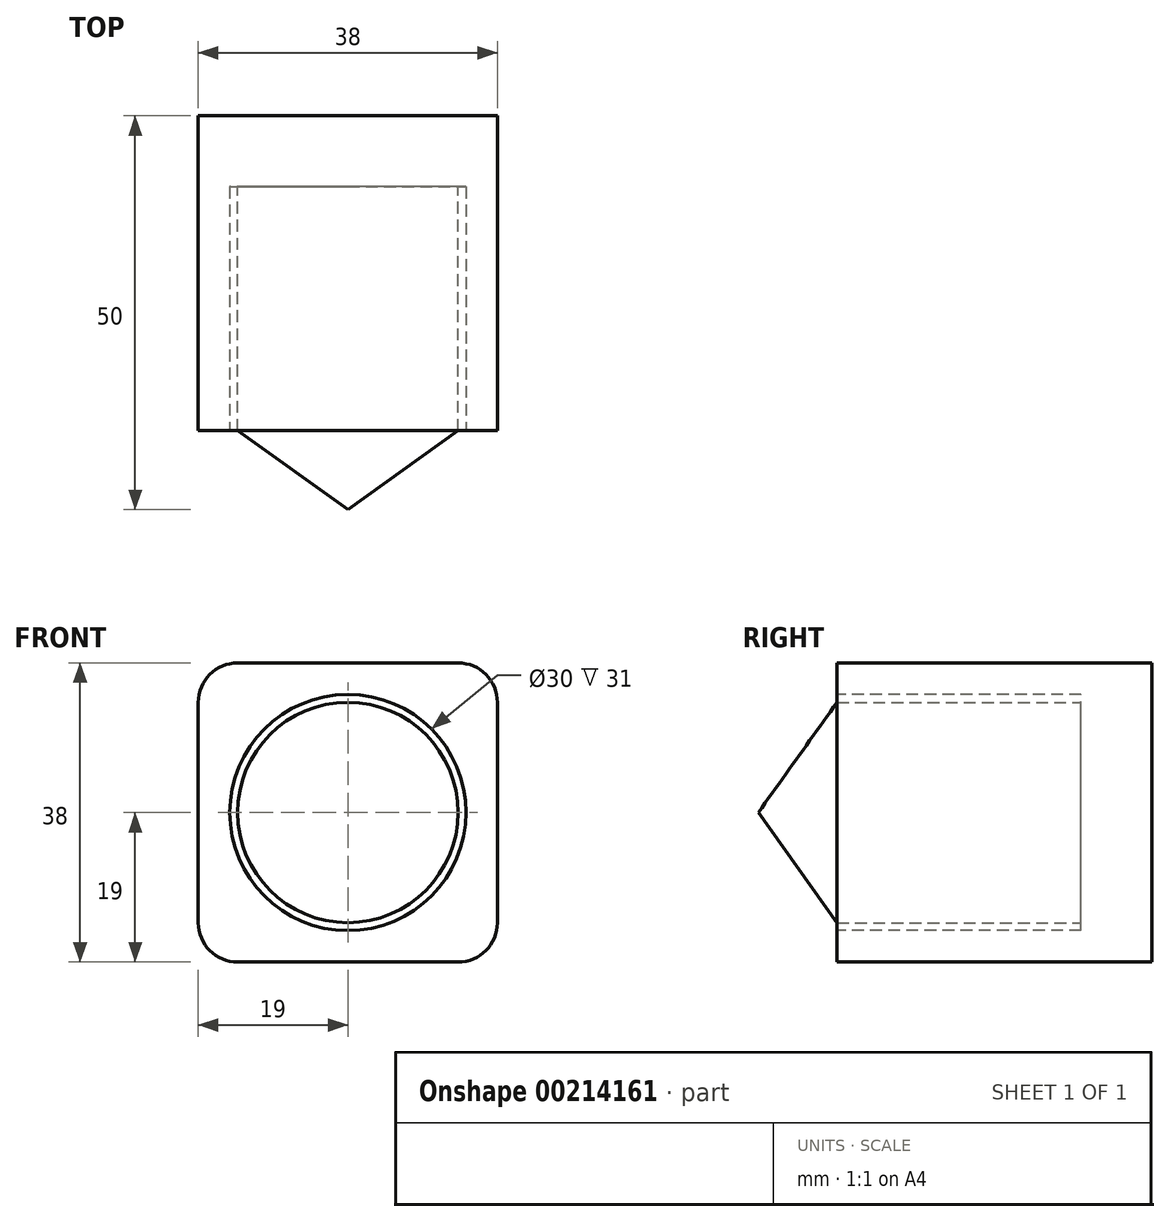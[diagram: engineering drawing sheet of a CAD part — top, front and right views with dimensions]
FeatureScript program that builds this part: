
annotation { "Feature Type Name" : "Feature", "Feature Type Description" : "" }
export const myFeature = defineFeature(function(context is Context, id is Id, definition is map)
    precondition{}
    {
        {
            var Q0;
            Q0=qCreatedBy(makeId("Front.planeOp"),FACE);
            var sketch = newSketch(context, id + "F0", { "sketchPlane" : qUnion([Q0])});
            skCircle(sketch, "E0.cCircle", {"center": v(0, 0) * mm, "radius": 19 * mm, "construction": true});
            skLineSegment(sketch, "E0.0", {"start": v(19, 19) * mm, "end": v(19, -19) * mm});
            skLineSegment(sketch, "E0.1", {"start": v(19, -19) * mm, "end": v(-19, -19) * mm});
            skLineSegment(sketch, "E0.2", {"start": v(-19, -19) * mm, "end": v(-19, 19) * mm});
            skLineSegment(sketch, "E0.3", {"start": v(-19, 19) * mm, "end": v(19, 19) * mm});
            skPoint(sketch, "E0.0.midPoint", {"position": v(19, 0) * mm});
            skSolve(sketch);
        }
        {
            var Q0;
            Q0=makeQuery(id+"F0.imprint","IMPRINT",FACE,{"disambiguationData":[TD([[makeQuery(id+"F0.imprint","IMPRINT",EDGE,{"derivedFrom":sQuery(id+"F0.wireOp",EDGE,"E0.0")}),-1.0]])]});
            extrude(context, id + "F1", {"entities" : qUnion([Q0]), "endBound" : BoundingType.SYMMETRIC, "depth" : 40 * mm});
        }
        {
            var Q0;
            Q0=makeQuery(id+"F1.opExtrude","CAP_FACE",FACE,{"disambiguationData":[OSD([sQuery(id+"F0.wireOp",EDGE,"E0.0"),sQuery(id+"F0.wireOp",EDGE,"E0.1"),sQuery(id+"F0.wireOp",EDGE,"E0.2"),sQuery(id+"F0.wireOp",EDGE,"E0.3")])],"isStart":false});
            var sketch = newSketch(context, id + "F2", { "sketchPlane" : qUnion([Q0])});
            skCircle(sketch, "E1", {"center": v(0, 0) * mm, "radius": 15 * mm});
            skSolve(sketch);
        }
        {
            var Q0;
            Q0=makeQuery(id+"F2.imprint","IMPRINT",FACE,{"disambiguationData":[TD([[makeQuery(id+"F2.imprint","IMPRINT",EDGE,{"derivedFrom":sQuery(id+"F2.wireOp",EDGE,"E1")}),1.0]])]});
            extrude(context, id + "F3", {"entities" : qUnion([Q0]), "operationType" : NewBodyOperationType.REMOVE, "oppositeDirection" : true, "depth" : 31 * mm});
        }
        {
            var Q0;
            Q0=makeQuery(id+"F1.opExtrude","SWEPT_EDGE",EDGE,{"disambiguationData":[OSD([sQuery(id+"F0.wireOp",EDGE,"E0.0"),sQuery(id+"F0.wireOp",EDGE,"E0.1")])]});
            var Q1;
            Q1=makeQuery(id+"F1.opExtrude","SWEPT_EDGE",EDGE,{"disambiguationData":[OSD([sQuery(id+"F0.wireOp",EDGE,"E0.0"),sQuery(id+"F0.wireOp",EDGE,"E0.3")])]});
            var Q2;
            Q2=makeQuery(id+"F1.opExtrude","SWEPT_EDGE",EDGE,{"disambiguationData":[OSD([sQuery(id+"F0.wireOp",EDGE,"E0.1"),sQuery(id+"F0.wireOp",EDGE,"E0.2")])]});
            var Q3;
            Q3=makeQuery(id+"F1.opExtrude","SWEPT_EDGE",EDGE,{"disambiguationData":[OSD([sQuery(id+"F0.wireOp",EDGE,"E0.2"),sQuery(id+"F0.wireOp",EDGE,"E0.3")])]});
            fillet(context, id + "F4", {"entities" : qUnion([Q0, Q1, Q2, Q3]), "radius" : 5 * mm, "tangentPropagation" : true, "allowEdgeOverflow" : false});
        }
        {
            var Q0;
            Q0=makeQuery(id+"F3.boolean.opBoolean","COPY",FACE,{"derivedFrom":makeQuery(id+"F3.opExtrude","CAP_FACE",FACE,{"disambiguationData":[OSD([sQuery(id+"F2.wireOp",EDGE,"E1")])],"isStart":false})});
            var sketch = newSketch(context, id + "F5", { "sketchPlane" : qUnion([Q0])});
            skCircle(sketch, "E2.0", {"center": v(0, 0) * mm, "radius": 15 * mm, "construction": true});
            skCircle(sketch, "E3.0", {"center": v(0, 0) * mm, "radius": 14 * mm});
            skCircle(sketch, "E4.0", {"center": v(0, 0) * mm, "radius": 20 * mm, "construction": true});
            skSolve(sketch);
        }
        {
            var Q0;
            Q0=makeQuery(id+"F5.imprint","IMPRINT",FACE,{"disambiguationData":[TD([[makeQuery(id+"F5.imprint","IMPRINT",EDGE,{"derivedFrom":sQuery(id+"F5.wireOp",EDGE,"E3.0")}),1.0]])]});
            var Q1;
            Q1=makeQuery(id+"F1.opExtrude","CAP_FACE",FACE,{"disambiguationData":[OSD([sQuery(id+"F0.wireOp",EDGE,"E0.0"),sQuery(id+"F0.wireOp",EDGE,"E0.1"),sQuery(id+"F0.wireOp",EDGE,"E0.2"),sQuery(id+"F0.wireOp",EDGE,"E0.3")])],"isStart":false});
            extrude(context, id + "F6", {"entities" : qUnion([Q0]), "endBound" : BoundingType.UP_TO_SURFACE, "endBoundEntityFace" : qUnion([Q1]), "depth" : 23 * mm});
        }
        {
            var Q0;
            Q0=qCreatedBy(makeId("Top.planeOp"),FACE);
            var sketch = newSketch(context, id + "F7", { "sketchPlane" : qUnion([Q0])});
            skLineSegment(sketch, "E5.0.0", {"start": v(14, -20) * mm, "end": v(-14, -20) * mm});
            skLineSegment(sketch, "E6", {"start": v(14, -20) * mm, "end": v(0, -30) * mm});
            skLineSegment(sketch, "E7", {"start": v(0, -30) * mm, "end": v(0, -20) * mm});
            skLineSegment(sketch, "E8", {"start": v(0, -20) * mm, "end": v(-9.2, -20) * mm});
            skSolve(sketch);
        }
        {
            var Q0;
            {var subQ0=sQuery(id+"F7.wireOp",EDGE,"E6");Q0=makeQuery(id+"F7.imprint","IMPRINT",FACE,{"disambiguationData":[TD([[makeQuery(id+"F7.imprint","IMPRINT",EDGE,{"derivedFrom":subQ0}),-1.0]])]});}
            var Q1;
            Q1=makeQuery(id+"F6.opExtrude","CAP_EDGE",EDGE,{"disambiguationData":[OSD([sQuery(id+"F5.wireOp",EDGE,"E3.0")])],"isStart":false});
            revolve(context, id + "F8", {"operationType" : NewBodyOperationType.ADD, "entities" : qUnion([Q0]), "axis" : qUnion([Q1]), "revolveType" : RevolveType.FULL});
        }
    });
